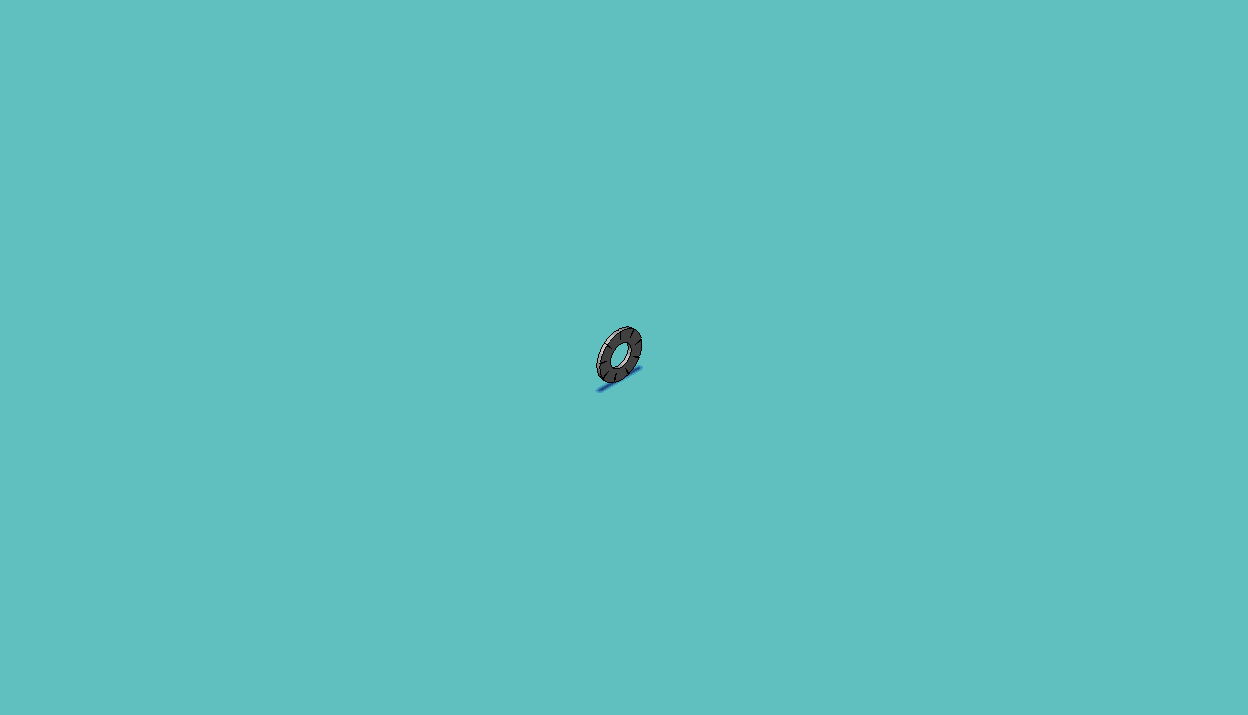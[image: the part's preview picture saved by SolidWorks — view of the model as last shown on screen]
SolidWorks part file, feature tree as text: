
SOLIDWORKS PART (.sldprt)
format: sldprt  version: not decoded by parser v0  size: 211,456 bytes
history: native  units: mm
features: sketch x7, plane x6, mirror x2, pattern_circular x2, material x1, extrude x1 + 2 further entries (+11 scaffold rows collapsed; 1 parser-record rows omitted)
feature tree (33):
  scaffold x11  (default folders/planes/origin — collapsed)
  material  "Material <not specified>"
  plane  "Plane1"
  plane  "Plane2"
  plane  "Plane3"
  parser-record x1  (decoder bookkeeping rows leaked as tree rows — omitted from the tree; the rows remain in map.json)
  extrude  "Base-Extrude"  [1 undecoded]
  sketch  "Sketch1"  dims[InsideDia=2.7mm OutsideDia=5.5mm Thickness=0.4mm D2=10.0mm D3=1.0deg D4=1.0deg]
  mirror  "TypeA2"
  sketch  "Sketch4"  dims[D1=0.1mm D2=0.1mm]
  sketch  "Sketch3"  dims[D1=1.812mm]
  sketch  "Sketch5"
  pattern_circular  "TypeAPattern"  Count=9 Angle=360deg NumTeeth=9
  plane  "Plane4"  Offset=2.75mm
  plane  "Plane5"  Offset=0.2mm
  plane  "Plane6"  Offset=1.2825mm
  sketch  "Sketch6"  dims[D1=2.274mm]
  sketch  "Sketch7"  dims[D1=0.1mm D2=0.1mm]
  sketch  "Sketch8"
  mirror  "TypeJ3"
  pattern_circular  "TypeJPattern"  Count=7 Angle=360deg NumTeeth=7
  "ConfigurationName"  CopiedFlag=1
  "ConfigurationName"  CopiedFlag=0
decode coverage: 7 of 12 modeling features carry decoded parameters; 2 rows unclassified (native names shown)
note: 1 parameter value undecoded
note: suppression state not decoded; provenance and decode notes live in map.json
